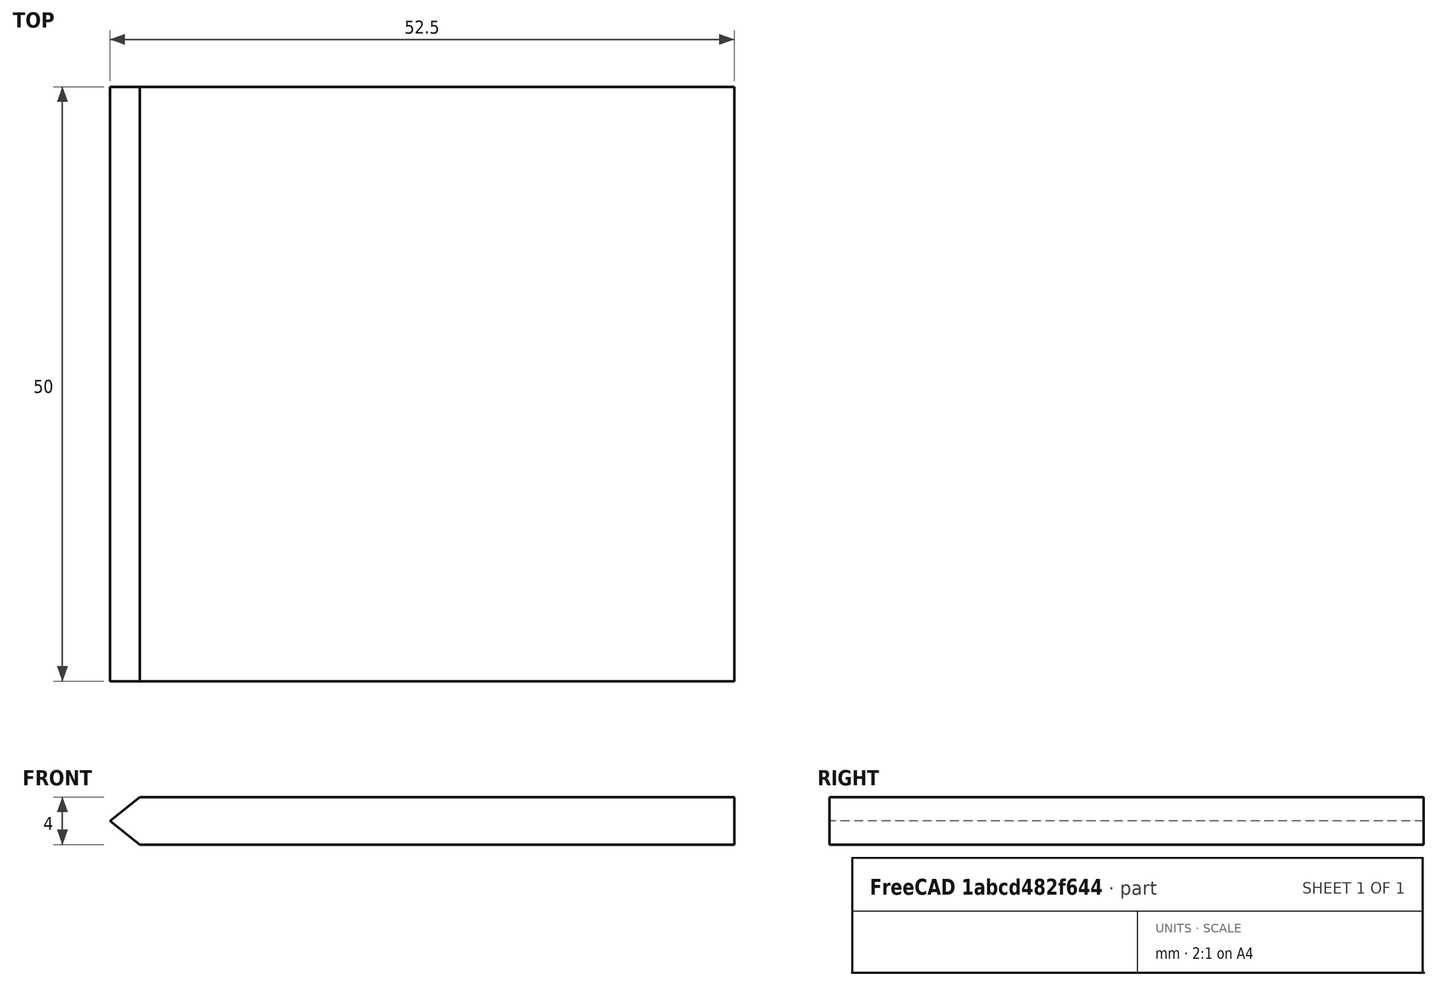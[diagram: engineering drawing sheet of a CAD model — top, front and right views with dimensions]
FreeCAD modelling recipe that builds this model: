
FCSTD DOCUMENT  (FreeCAD 2024.2R37179 (Git))
Label: Sand-Paper-Groove-Tool
License: All rights reserved
LicenseURL: https://en.wikipedia.org/wiki/All_rights_reserved
objects: Sketcher::SketchObject×1, PartDesign::Pad×1, PartDesign::Body×1
note: 4 computed .brp shape members not serialized (recipe doc carries the construction recipe); baked Part::Feature solids carry a one-line shape summary decoded from their .brp

FEATURE [Sketcher::SketchObject] Sketch
  AttachmentSupport = -> [XZ_Plane]
  FullyConstrained = true
  MapMode = 5
  Placement = pos=(0,0,0) rot=(1,0,0;1.5708rad)
  sketch-geometry (5):
    g0: LineSegment StartX=0 StartY=0 StartZ=0 EndX=-2.5 EndY=2 EndZ=0
    g1: LineSegment StartX=-2.5 StartY=2 StartZ=0 EndX=0 EndY=4 EndZ=0
    g2: LineSegment StartX=0 StartY=4 StartZ=0 EndX=50 EndY=4 EndZ=0
    g3: LineSegment StartX=50 StartY=4 StartZ=0 EndX=50 EndY=0 EndZ=0
    g4: LineSegment StartX=50 StartY=0 StartZ=0 EndX=0 EndY=0 EndZ=0
  constraints (14):
    c: Coincident(g-1,g0)
    c: Coincident(g0,g1)
    c: Coincident(g1,g2)
    c: Horizontal(g2)
    c: Coincident(g2,g3)
    c: PointOnObject(g3,g-1)
    c: Vertical(g3)
    c: Coincident(g3,g4)
    c: Coincident(g4,g0)
    c: DistanceY(g3,g3) = 4
    c: DistanceX(g2,g2) = 50
    c: PointOnObject(g1,g-2)
    c: DistanceX(g0,g0) = 2.5
    c: DistanceY(g0,g0) = 2
FEATURE [PartDesign::Pad] Pad
  Direction = (0,-1,2e-16)
  Length = 50
  Length2 = 10
  Placement = pos=(0,0,0) rot=(1,0,0;1.5708rad)
  Profile = -> Sketch
  ReferenceAxis = -> Sketch [N_Axis]
  Refine = true
  Suppressed = false
  Type = 0
FEATURE [PartDesign::Body] Body
  Group = -> [Sketch,Pad]
  Origin = -> Origin
  Tip = -> Pad
